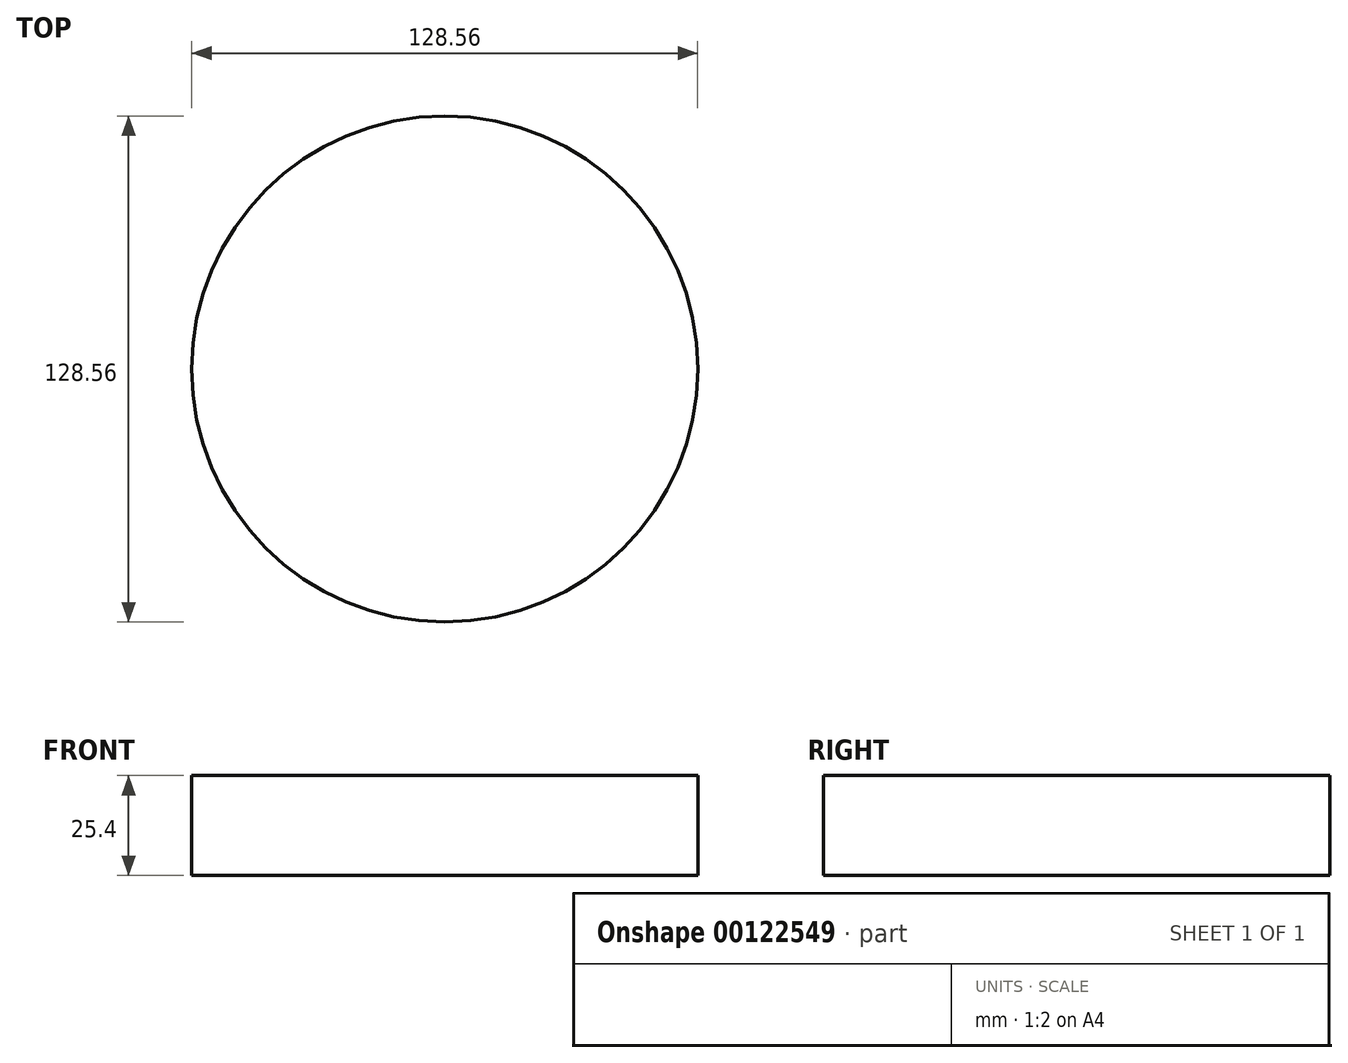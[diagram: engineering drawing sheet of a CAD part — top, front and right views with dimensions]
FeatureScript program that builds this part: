
annotation { "Feature Type Name" : "Feature", "Feature Type Description" : "" }
export const myFeature = defineFeature(function(context is Context, id is Id, definition is map)
    precondition{}
    {
        {
            var Q0;
            Q0=qCreatedBy(makeId("Top.planeOp"),FACE);
            var sketch = newSketch(context, id + "F1", { "sketchPlane" : qUnion([Q0])});
            skCircle(sketch, "E0", {"center": v(0, 0) * mm, "radius": 64.28 * mm});
            skSolve(sketch);
        }
        {
            var Q0;
            Q0=makeQuery(id+"F1.imprint","IMPRINT",FACE,{"disambiguationData":[TD([[makeQuery(id+"F1.imprint","IMPRINT",EDGE,{"derivedFrom":sQuery(id+"F1.wireOp",EDGE,"E0")}),1.0]])]});
            extrude(context, id + "F0", {"entities" : qUnion([Q0]), "depth" : 25.4 * mm});
        }
    });
